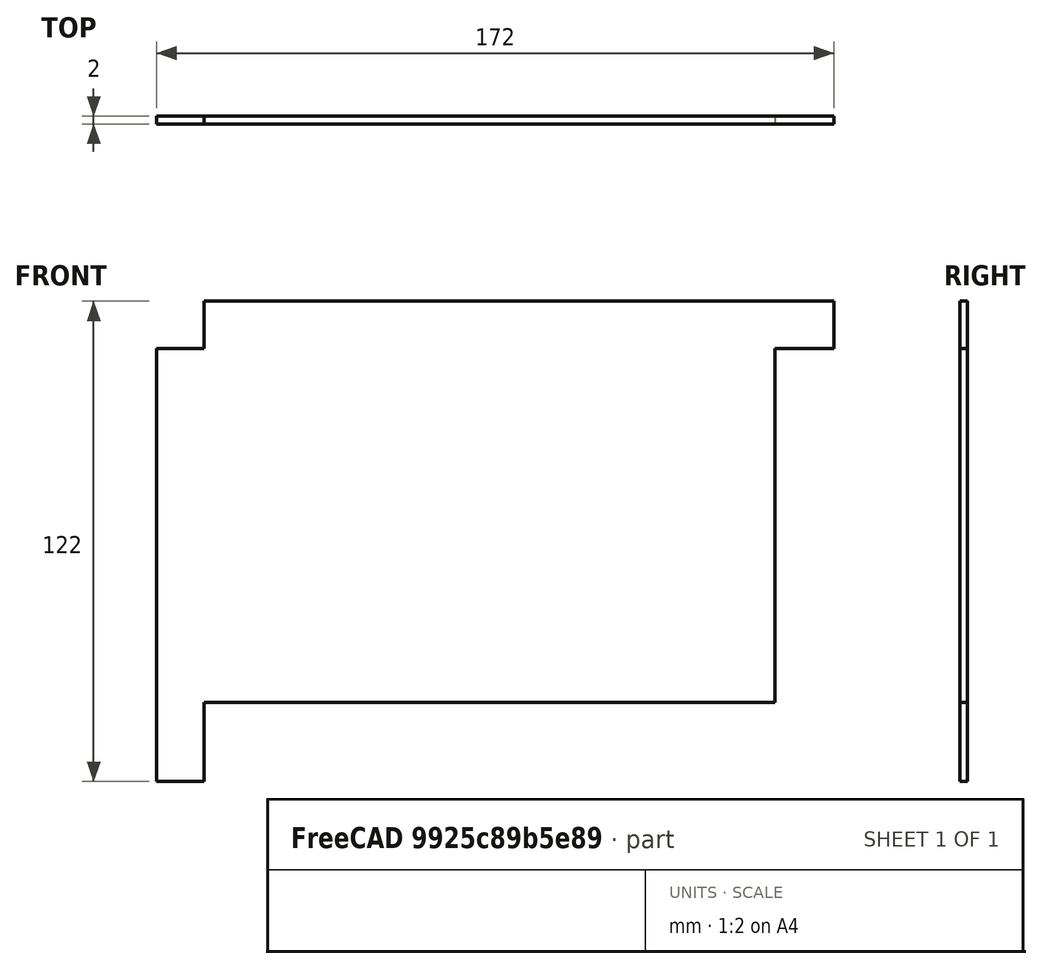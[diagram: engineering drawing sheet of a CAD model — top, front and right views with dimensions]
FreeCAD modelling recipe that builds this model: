
FCSTD DOCUMENT  (FreeCAD 0.19R24291 (Git))
Label: 8000_Profile_Template
License: All rights reserved
LicenseURL: http://en.wikipedia.org/wiki/All_rights_reserved
objects: TechDraw::DrawViewDimension×6, Sketcher::SketchObject×1, PartDesign::Pad×1, PartDesign::Body×1, TechDraw::DrawSVGTemplate×1, TechDraw::DrawViewPart×1, TechDraw::DrawPage×1
note: 4 computed .brp shape members not serialized (recipe doc carries the construction recipe); baked Part::Feature solids carry a one-line shape summary decoded from their .brp

FEATURE [Sketcher::SketchObject] Sketch
  FullyConstrained = false
  MapMode = 5
  Placement = pos=(0,0,0) rot=(1,0,0;1.5708rad)
  Support = -> [XZ_Plane]
  sketch-geometry (10):
    g0: LineSegment StartX=-0.507831 StartY=0.0298033 StartZ=0 EndX=-0.507831 EndY=110.03 EndZ=0
    g1: LineSegment StartX=-0.507831 StartY=0.0298033 StartZ=0 EndX=11.4922 EndY=0.0298033 EndZ=0
    g2: LineSegment StartX=11.4922 StartY=0.0298033 StartZ=0 EndX=11.4922 EndY=20.0298 EndZ=0
    g3: LineSegment StartX=11.4922 StartY=20.0298 StartZ=0 EndX=156.492 EndY=20.0298 EndZ=0
    g4: LineSegment StartX=156.492 StartY=20.0298 StartZ=0 EndX=156.492 EndY=110.03 EndZ=0
    g5: LineSegment StartX=156.492 StartY=110.03 StartZ=0 EndX=171.492 EndY=110.03 EndZ=0
    g6: LineSegment StartX=171.492 StartY=110.03 StartZ=0 EndX=171.492 EndY=122.03 EndZ=0
    g7: LineSegment StartX=171.492 StartY=122.03 StartZ=0 EndX=11.4922 EndY=122.03 EndZ=0
    g8: LineSegment StartX=-0.507831 StartY=110.03 StartZ=0 EndX=11.4922 EndY=110.03 EndZ=0
    g9: LineSegment StartX=11.4922 StartY=110.03 StartZ=0 EndX=11.4922 EndY=122.03 EndZ=0
  constraints (29):
    c: Vertical(g0)
    c: DistanceY(g0,g0) = 110
    c: Coincident(g1,g0)
    c: Horizontal(g1)
    c: Coincident(g2,g1)
    c: Vertical(g2)
    c: Coincident(g3,g2)
    c: Horizontal(g3)
    c: Coincident(g4,g3)
    c: Vertical(g4)
    c: Coincident(g5,g4)
    c: Horizontal(g5)
    c: Coincident(g6,g5)
    c: Vertical(g6)
    c: Horizontal(g7)
    c: DistanceX(g0,g1) = 12
    c: DistanceY(g3,g4) = 90
    c: DistanceY(g1,g2) = 20
    c: Coincident(g8,g0)
    c: Horizontal(g8)
    c: Coincident(g9,g8)
    c: Coincident(g9,g7)
    c: Vertical(g9)
    c: DistanceY(g6,g6) = 12
    c: Equal(g1,g8)
    c: Horizontal(g4,g8)
    c: DistanceX(g2,g3) = 145
    c: DistanceX(g7,g6) = 160
    c: Coincident(g6,g7)
FEATURE [PartDesign::Pad] Pad
  Direction = (1,1,1)
  Length = 2
  Length2 = 100
  Placement = pos=(0,0,0) rot=(1,0,0;1.5708rad)
  Profile = -> Sketch
  Type = 0
FEATURE [PartDesign::Body] Body
  Group = -> [Sketch,Pad]
  Origin = -> Origin
  Tip = -> Pad
FEATURE [TechDraw::DrawSVGTemplate] Template
  EditableTexts = Designed_by_Name=RIP; Drawing_number=8000_Profile_Template; FC-Date=Date; FC-SC=1:1; FC-SH=Sheet; FC-Title=Keyboard Template; Subtitle=Printable; Weight=-
  Height = 210
  Orientation = 1
  Width = 297
FEATURE [TechDraw::DrawViewPart] View
  CoarseView = false
  Direction = (0,-1,0)
  Focus = 100
  HardHidden = false
  IsoCount = 0
  IsoHidden = false
  IsoVisible = false
  LockPosition = false
  Perspective = false
  Rotation = 0
  ScaleType = 0
  SeamHidden = false
  SeamVisible = true
  SmoothHidden = false
  SmoothVisible = true
  Source = -> [Template,Pad]
  X = 125.167
  XDirection = (0.866,0.5,0)
  Y = 122.642
FEATURE [TechDraw::DrawViewDimension] Dimension
  Arbitrary = false
  ArbitraryTolerances = false
  EqualTolerance = true
  FormatSpec = %.2f
  FormatSpecOverTolerance = %+.2f
  FormatSpecUnderTolerance = %+.2f
  Inverted = false
  LockPosition = false
  MeasureType = 1
  OverTolerance = 0
  References2D = -> [View]
  Rotation = 0
  ScaleType = 0
  TheoreticalExact = false
  Type = 2
  UnderTolerance = 0
  X = 109.768
  Y = 55
FEATURE [TechDraw::DrawViewDimension] Dimension001
  Arbitrary = false
  ArbitraryTolerances = false
  EqualTolerance = true
  FormatSpec = %.2f
  FormatSpecOverTolerance = %+.2f
  FormatSpecUnderTolerance = %+.2f
  Inverted = false
  LockPosition = false
  MeasureType = 1
  OverTolerance = 0
  References2D = -> [View]
  Rotation = 0
  ScaleType = 0
  TheoreticalExact = false
  Type = 2
  UnderTolerance = 0
  X = 95.3726
  Y = 3.43089
FEATURE [TechDraw::DrawViewDimension] Dimension003
  Arbitrary = false
  ArbitraryTolerances = false
  EqualTolerance = true
  FormatSpec = %.2f
  FormatSpecOverTolerance = %+.2f
  FormatSpecUnderTolerance = %+.2f
  Inverted = false
  LockPosition = false
  MeasureType = 1
  OverTolerance = 0
  References2D = -> [View]
  Rotation = 0
  ScaleType = 0
  TheoreticalExact = false
  Type = 1
  UnderTolerance = 0
  X = -82.4267
  Y = -79.7805
FEATURE [TechDraw::DrawViewDimension] Dimension004
  Arbitrary = false
  ArbitraryTolerances = false
  EqualTolerance = true
  FormatSpec = %.2f
  FormatSpecOverTolerance = %+.2f
  FormatSpecUnderTolerance = %+.2f
  Inverted = false
  LockPosition = false
  MeasureType = 1
  OverTolerance = 0
  References2D = -> [View]
  Rotation = 0
  ScaleType = 0
  TheoreticalExact = false
  Type = 2
  UnderTolerance = 0
  X = -105.784
  Y = -3.15447
FEATURE [TechDraw::DrawViewDimension] Dimension005
  Arbitrary = false
  ArbitraryTolerances = false
  EqualTolerance = true
  FormatSpec = %.2f
  FormatSpecOverTolerance = %+.2f
  FormatSpecUnderTolerance = %+.2f
  Inverted = false
  LockPosition = false
  MeasureType = 1
  OverTolerance = 0
  References2D = -> [View]
  Rotation = 0
  ScaleType = 0
  TheoreticalExact = false
  Type = 1
  UnderTolerance = 0
  X = -10.0189
  Y = -45.8374
FEATURE [TechDraw::DrawViewDimension] Dimension006
  Arbitrary = false
  ArbitraryTolerances = false
  EqualTolerance = true
  FormatSpec = %.2f
  FormatSpecOverTolerance = %+.2f
  FormatSpecUnderTolerance = %+.2f
  Inverted = false
  LockPosition = false
  MeasureType = 1
  OverTolerance = 0
  References2D = -> [View]
  Rotation = 0
  ScaleType = 0
  TheoreticalExact = false
  Type = 1
  UnderTolerance = 0
  X = 7.42276
  Y = 74.374
FEATURE [TechDraw::DrawPage] Page
  KeepUpdated = true
  NextBalloonIndex = 1
  ProjectionType = 0
  Template = -> Template
  Views = -> [View,Dimension,Dimension001,Dimension003,Dimension004,Dimension005,Dimension006]
